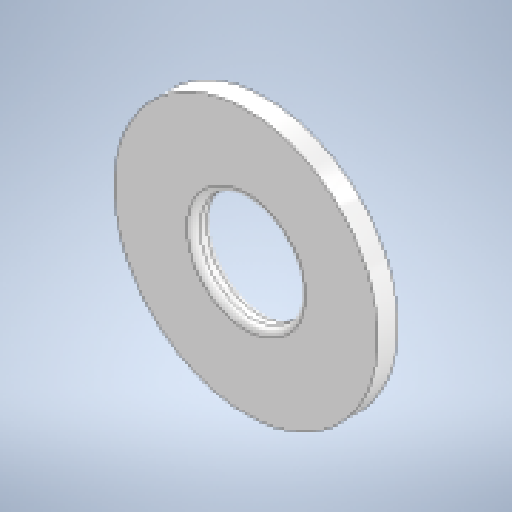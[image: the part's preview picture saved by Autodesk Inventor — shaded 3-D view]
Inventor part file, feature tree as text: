
AUTODESK INVENTOR PART (.ipt)
format: ipt  version: 2025.1 (Build 291241000, 241)  size: 146,432 bytes
history: native  units: mm
features: other x5, sketch x1, extrude x1, fillet x1, reference x1
ambient origin geometry x8: Origin, YZ Plane, XZ Plane, XY Plane, X Axis, Y Axis, Z Axis, Center Point
bodies: Body1 (feature_tree)
feature tree (9):
  other  "ソリッド1"
  sketch  "スケッチ1"
  other  "作業平面1"
  extrude  "押し出し1"  Depth=40.0mm
  fillet  "フィレット1"  Radius=10.0mm
  reference  "参照1"
  other  "<userpath>\Documents\Inventor\Vixen\doutai.iam"
  other  "doutai.iam"
  other  "02157_SmallDiameterHornB:2"
